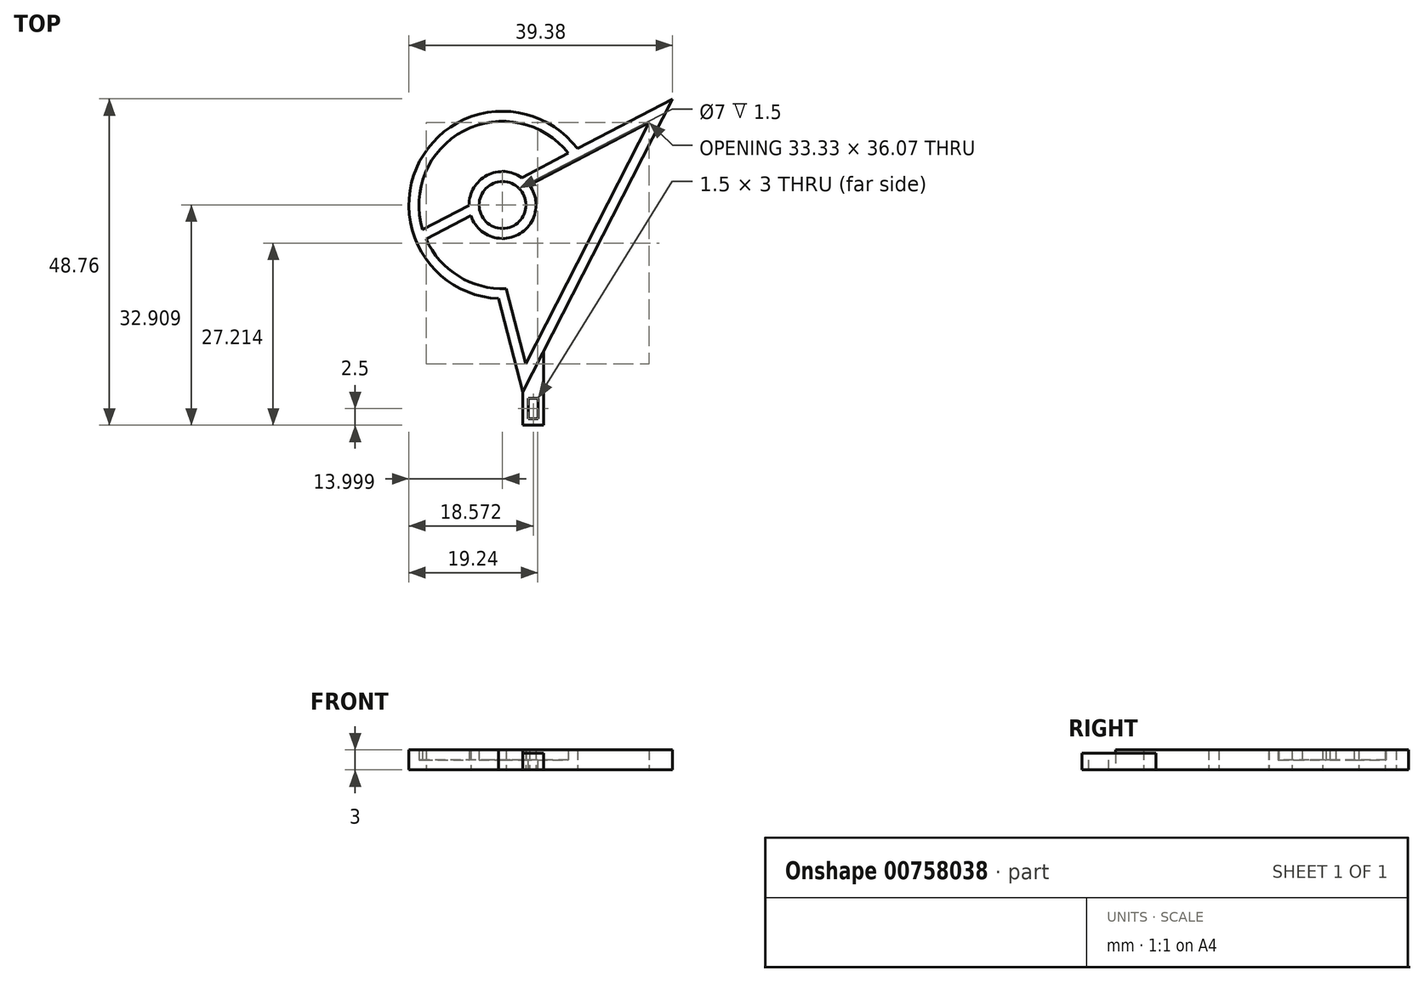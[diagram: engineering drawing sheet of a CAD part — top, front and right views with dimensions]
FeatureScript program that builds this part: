
annotation { "Feature Type Name" : "Feature", "Feature Type Description" : "" }
export const myFeature = defineFeature(function(context is Context, id is Id, definition is map)
    precondition{}
    {
        {
            var Q0;
            Q0=qCreatedBy(makeId("Front.planeOp"),FACE);
            var sketch = newSketch(context, id + "F0", { "sketchPlane" : qUnion([Q0])});
            skLineSegment(sketch, "E0", {"start": v(-25, 0) * mm, "end": v(25, 0) * mm, "construction": true});
            skLineSegment(sketch, "E1", {"start": v(0, 25) * mm, "end": v(0, -25) * mm, "construction": true});
            skArc(sketch, "E2", {"start": v(-17.53, 1) * mm, "mid": v(-12.7, -4.54) * mm, "end": v(-5.58, -6.4) * mm});
            skArc(sketch, "E3", {"start": v(-10.85, 4.5) * mm, "mid": v(-3.8, 1.65) * mm, "end": v(-2.1, 9.07) * mm});
            skCircle(sketch, "E4", {"center": v(-6.11, 6.08) * mm, "radius": 3.5 * mm});
            skLineSegment(sketch, "E5", {"start": v(-6.74, -7.9) * mm, "end": v(-3.07, -21.83) * mm});
            skLineSegment(sketch, "E6", {"start": v(-3.07, -21.83) * mm, "end": v(19.27, 21.93) * mm});
            skLineSegment(sketch, "E7", {"start": v(-17.53, 1) * mm, "end": v(-10.85, 4.5) * mm});
            skPoint(sketch, "E8.orphan", {"position": v(4.97, 11.87) * mm});
            skPoint(sketch, "E9.start.orphan", {"position": v(-17.19, 0.29) * mm});
            skLineSegment(sketch, "E10", {"start": v(-18.06, 2.42) * mm, "end": v(-11.11, 6.05) * mm});
            skLineSegment(sketch, "E11", {"start": v(5.07, 14.5) * mm, "end": v(19.27, 21.93) * mm});
            skLineSegment(sketch, "E12", {"start": v(-5.2, -7.89) * mm, "end": v(-2.62, -17.65) * mm});
            skLineSegment(sketch, "E13", {"start": v(-2.62, -17.65) * mm, "end": v(-5.58, -6.4) * mm});
            skLineSegment(sketch, "E14", {"start": v(4.58, 12.56) * mm, "end": v(15.8, 18.42) * mm});
            skLineSegment(sketch, "E15", {"start": v(-1.78, -16) * mm, "end": v(2.08, -8.43) * mm});
            skLineSegment(sketch, "E16", {"start": v(2.08, -8.43) * mm, "end": v(-2.62, -17.65) * mm});
            skLineSegment(sketch, "E17", {"start": v(2.08, -8.43) * mm, "end": v(15.8, 18.42) * mm});
            skArc(sketch, "E18.trimOffspring", {"start": v(5.07, 14.5) * mm, "mid": v(-18.5, 12.6) * mm, "end": v(-6.74, -7.9) * mm});
            skArc(sketch, "E19.trimOffspring", {"start": v(3.72, 13.8) * mm, "mid": v(-11.9, 17.16) * mm, "end": v(-18.06, 2.42) * mm});
            skLineSegment(sketch, "E20.trimOffspring", {"start": v(-3.23, 10.17) * mm, "end": v(3.72, 13.8) * mm});
            skLineSegment(sketch, "E21.trimOffspring", {"start": v(-2.1, 9.07) * mm, "end": v(4.58, 12.56) * mm});
            skArc(sketch, "E22.trimOffspring", {"start": v(-3.23, 10.17) * mm, "mid": v(-8.43, 10.51) * mm, "end": v(-11.11, 6.05) * mm});
            skLineSegment(sketch, "E23", {"start": v(-3.07, -21.83) * mm, "end": v(-3.07, -26.83) * mm});
            skLineSegment(sketch, "E24", {"start": v(-3.07, -26.83) * mm, "end": v(0, -26.83) * mm});
            skLineSegment(sketch, "E25", {"start": v(0, -26.83) * mm, "end": v(0, -15.8) * mm});
            skSolve(sketch);
        }
        {
            var Q0;
            {var subQ8=sQuery(id+"F0.wireOp",EDGE,"E2");Q0=makeQuery(id+"F0.imprint","IMPRINT",FACE,{"disambiguationData":[TD([[makeQuery(id+"F0.imprint","IMPRINT",EDGE,{"derivedFrom":subQ8}),-1.0]])]});}
            var Q1;
            Q1=sQuery(id+"F0.wireOp",EDGE,"E18.trimOffspring");
            var Q2;
            Q2=sQuery(id+"F0.wireOp",EDGE,"E5");
            var Q3;
            Q3=sQuery(id+"F0.wireOp",EDGE,"E6");
            var Q4;
            Q4=sQuery(id+"F0.wireOp",EDGE,"E13");
            var Q5;
            Q5=sQuery(id+"F0.wireOp",EDGE,"E16");
            var Q6;
            Q6=sQuery(id+"F0.wireOp",EDGE,"E17");
            var Q7;
            Q7=sQuery(id+"F0.wireOp",EDGE,"E2");
            var Q8;
            Q8=sQuery(id+"F0.wireOp",EDGE,"E7");
            var Q9;
            Q9=sQuery(id+"F0.wireOp",EDGE,"E19.trimOffspring");
            var Q10;
            Q10=sQuery(id+"F0.wireOp",EDGE,"E10");
            var Q11;
            Q11=sQuery(id+"F0.wireOp",EDGE,"E3");
            var Q12;
            Q12=sQuery(id+"F0.wireOp",EDGE,"E22.trimOffspring");
            var Q13;
            Q13=sQuery(id+"F0.wireOp",EDGE,"E4");
            var Q14;
            Q14=sQuery(id+"F0.wireOp",EDGE,"E21.trimOffspring");
            var Q15;
            Q15=sQuery(id+"F0.wireOp",EDGE,"E20.trimOffspring");
            var Q16;
            Q16=sQuery(id+"F0.wireOp",EDGE,"E14");
            var Q17;
            Q17=sQuery(id+"F0.wireOp",EDGE,"E11");
            extrude(context, id + "F1", {"entities" : qUnion([Q0]), "surfaceEntities" : qUnion([Q1, Q2, Q3, Q4, Q5, Q6, Q7, Q8, Q9, Q10, Q11, Q12, Q13, Q14, Q15, Q16, Q17]), "depth" : 3 * mm, "offsetDistance" : 25 * mm});
        }
        {
            var Q0;
            Q0=makeQuery(id+"F0.imprint","IMPRINT",FACE,{"disambiguationData":[TD([[makeQuery(id+"F0.imprint","IMPRINT",EDGE,{"derivedFrom":sQuery(id+"F0.wireOp",EDGE,"E10")}),1.0]])]});
            var Q1;
            Q1=makeQuery(id+"F0.imprint","IMPRINT",FACE,{"disambiguationData":[TD([[makeQuery(id+"F0.imprint","IMPRINT",EDGE,{"derivedFrom":sQuery(id+"F0.wireOp",EDGE,"E4")}),1.0]])]});
            extrude(context, id + "F2", {"entities" : qUnion([Q0, Q1]), "operationType" : NewBodyOperationType.ADD, "depth" : 1.5 * mm, "offsetDistance" : 25 * mm});
        }
        {
            var Q0;
            {var subQ0=sQuery(id+"F0.wireOp",EDGE,"E23");Q0=makeQuery(id+"F0.imprint","IMPRINT",FACE,{"disambiguationData":[TD([[makeQuery(id+"F0.imprint","IMPRINT",EDGE,{"derivedFrom":subQ0}),1.0]])]});}
            extrude(context, id + "F3", {"entities" : qUnion([Q0]), "operationType" : NewBodyOperationType.ADD, "depth" : 2.5 * mm, "offsetDistance" : 25 * mm});
        }
        {
            var Q0;
            Q0=makeQuery(id+"F3.opExtrude","CAP_FACE",FACE,{"disambiguationData":[OSD([sQuery(id+"F0.wireOp",EDGE,"E6"),sQuery(id+"F0.wireOp",EDGE,"E23"),sQuery(id+"F0.wireOp",EDGE,"E24"),sQuery(id+"F0.wireOp",EDGE,"E25")])],"isStart":false});
            var sketch = newSketch(context, id + "F4", { "sketchPlane" : qUnion([Q0])});
            skLineSegment(sketch, "E26.bottom", {"start": v(-2.29, -25.83) * mm, "end": v(-0.79, -25.83) * mm});
            skLineSegment(sketch, "E26.top", {"start": v(-2.29, -22.83) * mm, "end": v(-0.79, -22.83) * mm});
            skLineSegment(sketch, "E26.left", {"start": v(-2.29, -25.83) * mm, "end": v(-2.29, -22.83) * mm});
            skLineSegment(sketch, "E26.right", {"start": v(-0.79, -25.83) * mm, "end": v(-0.79, -22.83) * mm});
            skSolve(sketch);
        }
        {
            var Q0;
            Q0 = qSketchRegion(id + "F4", true);
            extrude(context, id + "F5", {"entities" : qUnion([Q0]), "operationType" : NewBodyOperationType.REMOVE, "oppositeDirection" : true, "depth" : 25 * mm, "offsetDistance" : 25 * mm});
        }
        {
            var Q0;
            Q0=makeQuery(id+"F1.opExtrude","SWEPT_BODY",BODY,{"disambiguationData":[OSD([sQuery(id+"F0.wireOp",EDGE,"E2"),sQuery(id+"F0.wireOp",EDGE,"E3"),sQuery(id+"F0.wireOp",EDGE,"E4"),sQuery(id+"F0.wireOp",EDGE,"E5"),sQuery(id+"F0.wireOp",EDGE,"E6"),sQuery(id+"F0.wireOp",EDGE,"E7"),sQuery(id+"F0.wireOp",EDGE,"E10"),sQuery(id+"F0.wireOp",EDGE,"E11"),sQuery(id+"F0.wireOp",EDGE,"E13"),sQuery(id+"F0.wireOp",EDGE,"E14"),sQuery(id+"F0.wireOp",EDGE,"E16"),sQuery(id+"F0.wireOp",EDGE,"E17"),sQuery(id+"F0.wireOp",EDGE,"E18.trimOffspring"),sQuery(id+"F0.wireOp",EDGE,"E19.trimOffspring"),sQuery(id+"F0.wireOp",EDGE,"E20.trimOffspring"),sQuery(id+"F0.wireOp",EDGE,"E21.trimOffspring"),sQuery(id+"F0.wireOp",EDGE,"E22.trimOffspring")])]});
            var Q1;
            Q1=makeQuery(id+"F3.opExtrude","CAP_EDGE",EDGE,{"disambiguationData":[OSD([sQuery(id+"F0.wireOp",EDGE,"E24")])],"isStart":false});
            transform(context, id + "F6", {"entities" : qUnion([Q0]), "transformType" : TransformType.ROTATION, "transformAxis" : qUnion([Q1]), "angle" : 270 * degree, "makeCopy" : false});
        }
    });
